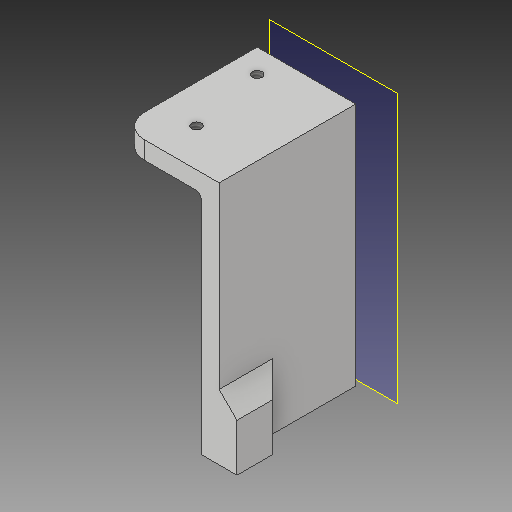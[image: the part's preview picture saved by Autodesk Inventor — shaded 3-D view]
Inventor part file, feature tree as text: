
AUTODESK INVENTOR PART (.ipt)
format: ipt  version: 2019 (Build 230136000, 136)  size: 200,704 bytes
history: native  units: in
note: dims shown in document units (in); Inventor stores cm internally (conversion verified against a paired STEP export)
features: sketch x6, projected_geometry x5, extrude x4, fillet x2, hole x2, chamfer x1, plane x1, mirror x1
ambient origin geometry x8: Origin, YZ Plane, XZ Plane, XY Plane, X Axis, Y Axis, Z Axis, Center Point
bodies: Solid1 (feature_tree)
feature tree (22):
  extrude  "Extrusion1"  Depth=0.636in
  extrude  "Extrusion3"  Depth=1.4375in
  extrude  "Extrusion4"  Depth=0.1875in TaperAngle=0.0deg
  fillet  "Fillet1"  Radius=1.25in
  extrude  "Extrusion5"  Depth=0.1875in TaperAngle=0.0deg
  chamfer  "Chamfer1"  Distance=0.375in
  hole  "Hole1"  [1 undecoded]
  hole  "Hole2"  [1 undecoded]
  fillet  "Fillet2"  Radius=0.5in
  plane  "Work Plane1"
  mirror  "Mirror1"
  sketch  "Sketch1"  dims[d0=2.57in d1=0.636in]
  sketch  "Sketch3"  dims[d4=0.1875in d5=0.0in d11=1.4375in]
  projected_geometry  "Projected Loop2"
  sketch  "Sketch4"  dims[d12=1.0375in d13=0.1875in d14=0.0in d15=1.25in]
  projected_geometry  "Projected Loop3"
  sketch  "Sketch6"  dims[d16=0.85in d17=0.1875in d18=0.0in]
  projected_geometry  "Projected Loop5"
  sketch  "Sketch8"  dims[d19=0.0625in]
  projected_geometry  "Projected Loop6"
  sketch  "Sketch9"  dims[d24=0.375in d25=0.375in d26=0.375in d27=0.375in d28=0.5in d29=0.0in d30=0.1875in d31=0.125in d32=45.0deg d33=0.104in d34=0.276in d35=0.375in d36=0.25in d37=0.5635in d38=0.5in d39=0.8108in d41=0.104in d42=0.276in d43=0.375in d44=0.25in d45=0.5635in d46=0.432in d47=0.8108in d50=1.25in d51=0.85in d52=0.25in d56=0.4in d57=0.25in d58=0.4in d59=0.25in]
  projected_geometry  "Projected Loop7"
note: 2 required parameter values undecoded (feature->parameter linkage not recoverable at this tier; creation-order binding heuristic only, values carry confidence <= 0.55)
